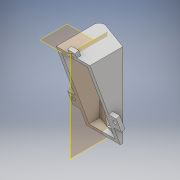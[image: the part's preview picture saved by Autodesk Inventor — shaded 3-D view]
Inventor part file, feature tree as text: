
AUTODESK INVENTOR PART (.ipt)
format: ipt  version: 2017 (Build 210142000, 142)  size: 203,264 bytes
history: native  units: mm
features: sketch x7, extrude x5, plane x2, hole x2, shell x1, fillet x1, mirror x1
ambient origin geometry x8: Origin, YZ Plane, XZ Plane, XY Plane, X Axis, Y Axis, Z Axis, Center Point
bodies: Body1 (feature_tree)
feature tree (19):
  plane  "Work Plane1"
  extrude  "Extrusion5"  Depth=19.198622mm
  extrude  "Extrusion6"  Depth=67.0mm
  shell  "Shell3"  Thickness=40.0mm
  extrude  "Extrusion7"  Depth=14.0mm
  fillet  "Fillet1"  Radius=55.0mm
  sketch  "Sketch10"  dims[d33=20.0mm d35=3.490659mm d37=20.0mm d39=3.490659mm]
  plane  "Work Plane2"
  extrude  "Extrusion8"  Depth=20.0mm
  hole  "Hole1"  [1 undecoded]
  mirror  "Mirror2"
  extrude  "Extrusion9"  Depth=4.0mm
  hole  "Hole2"  [1 undecoded]
  sketch  "Sketch7"  dims[d20=2.0mm d21=19.198622mm]
  sketch  "Sketch8"  dims[d24=67.0mm d25=0.0mm d27=3.490659mm d28=40.0mm d29=0.0mm]
  sketch  "Sketch9"  dims[d30=3.0mm d31=14.0mm d32=55.0mm]
  sketch  "Sketch11"  dims[d41=2.0mm d42=3.0mm]
  sketch  "Sketch12"  dims[d43=40.0mm d44=0.0mm d45=4.0mm]
  sketch  "Sketch13"  dims[d46=3.0mm d47=12.0mm d48=15.0mm d49=-13.5mm d50=6.0mm d51=0.0mm d52=5.0mm d53=3.0mm d54=3.0mm d55=6.0mm d56=4.0mm d57=2.0mm d58=90.0deg d59=8.0mm d60=20.594885mm d61=75.062956mm d62=6.0mm d64=10.5mm d65=3.0mm d66=0.0mm d67=3.0mm d68=3.0mm d69=3.0mm d70=6.0mm d71=4.0mm d72=2.0mm d73=90.0deg d74=8.0mm d75=20.594885mm d76=27.0mm]
note: 2 required parameter values undecoded (feature->parameter linkage not recoverable at this tier; creation-order binding heuristic only, values carry confidence <= 0.55)
